# Revit family: 150-BAÑERA ESMALT 150 X 70 ADBA
name_source: partatom
category: Aparatos sanitarios
units: mm (PartAtom-declared; Revit-internal decimal feet)

## family parameters
Compartido = No
Corte con vacíos al cargar = No
Cota de conector redondo = Radio de uso
Número OmniClass = 23.45.05.14.21.11
Punto de cálculo de habitación = No
Se basa en plano de trabajo = No
Siempre vertical = Sí
Tipo de pieza = Normal
Título OmniClass = Bath/Shower Units

## types (1)
- BAÑERA ESMALT 150 X 70 AD/BA
    Bath Tub Material = <Por categoría>
    CWFU = 1
    Cold Water Radius = 8 mm
    Elevación por defecto = 0 cm
    F_Alto = 39 cm
    F_Ancho = 150 cm
    F_Color = Acero esmaltado blanco
    F_Descripción = Tina de acero esmaltado, espesor comercial 1,9 mm
    F_Peso = 19.90 kgf
    F_Productos necesarios para instalación = Kit de desagüe y sifón para tina, soporte
    F_Profundidad = 70 cm
    F_SKU = SBAD48241301BL
    Faucet Material = <Por categoría>
    HWFU = 1
    Sanitary Radius = 20 mm
    URL = https://www.fanaloza.cl
    WFU = 2

## geometry (parser evidence)
native form markers: Sweep x2
no freeform markers — native parametric forms only
